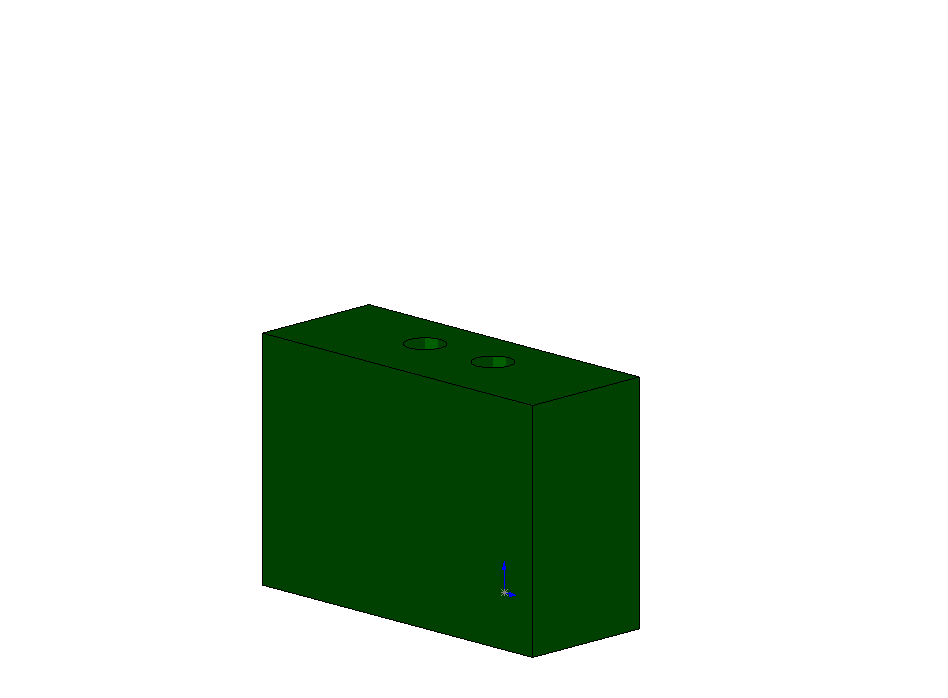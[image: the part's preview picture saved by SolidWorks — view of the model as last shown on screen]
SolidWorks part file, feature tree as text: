
SOLIDWORKS PART (.sldprt)
format: sldprt  version: not decoded by parser v0  size: 285,696 bytes
history: native  units: mm
features: sketch x4, material x1, extrude x1, cut_extrude x1, hole x1 + 1 further entry (+11 scaffold rows collapsed)
feature tree (20):
  scaffold x11  (default folders/planes/origin — collapsed)
  material  "Material <not specified>"
  "Origin"  ID=-1
  sketch  "Sketch1"  dims[D1=52.0mm D2=38.0mm]
  extrude  "Extrude1"  Depth=15mm
  sketch  "Sketch4"  dims[D1=26.0mm]
  cut_extrude  "Cut-Extrude3"  [1 undecoded]
  hole  "#8 Clearance Hole2"  Diameter=4.4958mm Depth=26mm
  sketch  "Sketch13"  dims[D1=9.525mm D2=6.35mm]
  sketch  "Sketch12"  dims[hole-wizard template sketch: 60 standard entries collapsed; hole parameters kept: c18.Thru Hole Depth=26.0mm]
decode coverage: 6 of 7 modeling features carry decoded parameters; 1 rows unclassified (native names shown)
note: ~ marks probable driven/reference dimensions
note: 1 parameter value undecoded
note: suppression state not decoded; provenance and decode notes live in map.json
